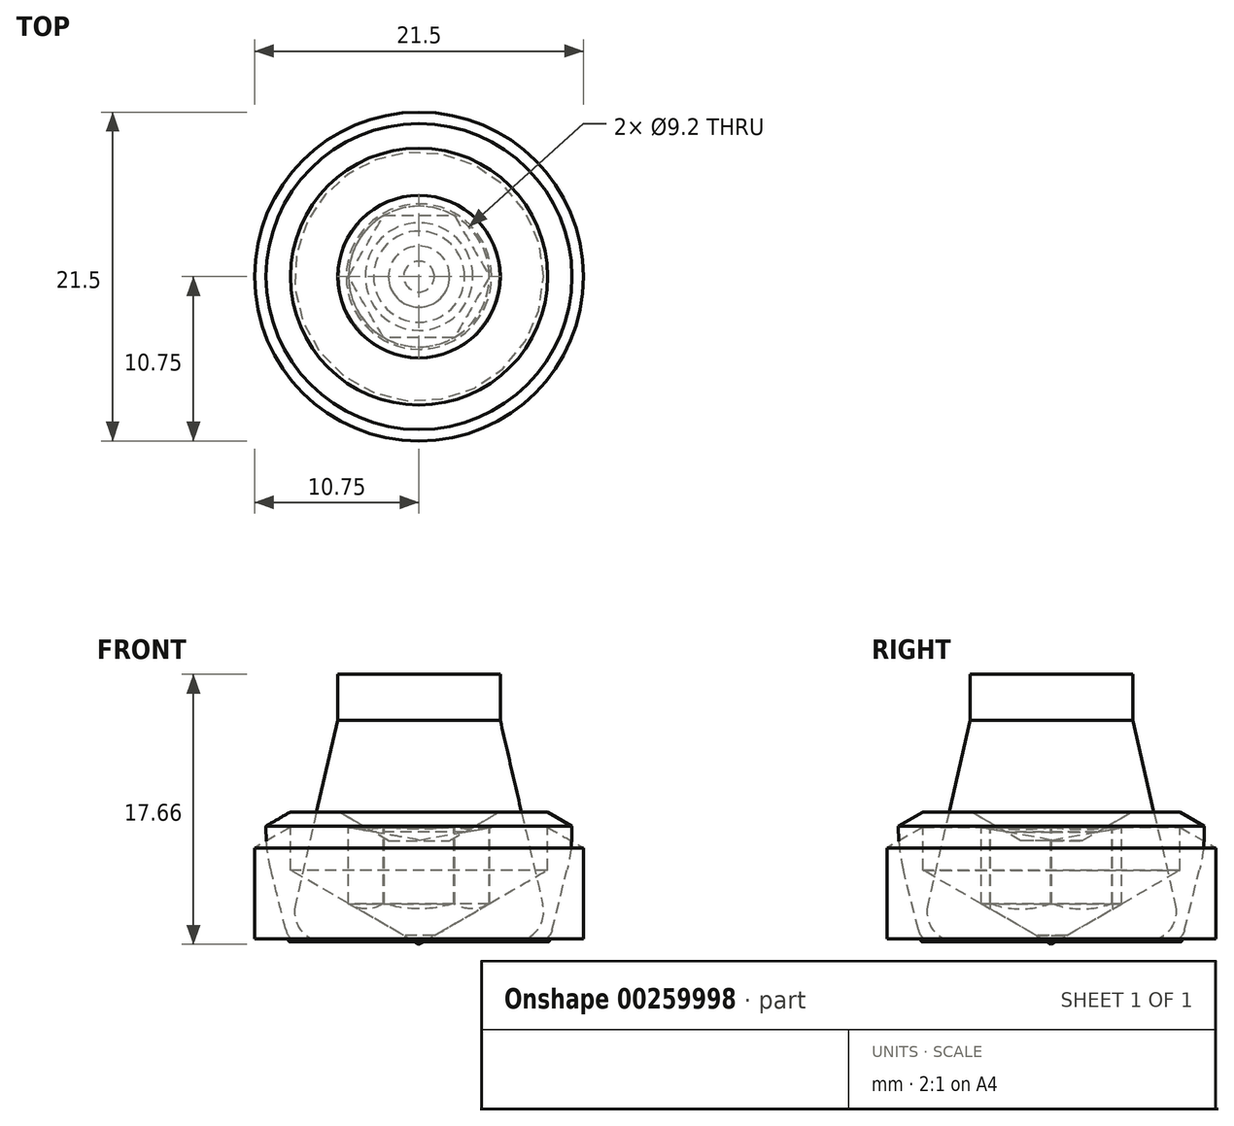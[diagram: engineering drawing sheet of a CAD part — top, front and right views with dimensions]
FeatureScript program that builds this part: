
annotation { "Feature Type Name" : "Feature", "Feature Type Description" : "" }
export const myFeature = defineFeature(function(context is Context, id is Id, definition is map)
    precondition{}
    {
        {
            var Q0;
            Q0=qCreatedBy(makeId("Front.planeOp"),FACE);
            var sketch = newSketch(context, id + "F0", { "sketchPlane" : qUnion([Q0])});
            skLineSegment(sketch, "E0", {"start": v(0, 0) * mm, "end": v(0, 0.42) * mm, "construction": true});
            skLineSegment(sketch, "E1", {"start": v(4.6, 7.5) * mm, "end": v(8.4, 7.5) * mm});
            skLineSegment(sketch, "E2", {"start": v(10.75, 6.14) * mm, "end": v(10.75, 0.2) * mm});
            skLineSegment(sketch, "E3", {"start": v(8.42, 0) * mm, "end": v(0, 0) * mm});
            skPoint(sketch, "E4.visualSharp", {"position": v(10.75, 7.5) * mm});
            skLineSegment(sketch, "E5", {"start": v(4.6, 7.5) * mm, "end": v(4.6, 2.5) * mm});
            skLineSegment(sketch, "E6", {"start": v(4.6, 2.5) * mm, "end": v(1, 0.42) * mm});
            skLineSegment(sketch, "E7", {"start": v(1, 0.42) * mm, "end": v(0, 0.42) * mm});
            skLineSegment(sketch, "E8", {"start": v(0, 0.42) * mm, "end": v(0, 0) * mm});
            skLineSegment(sketch, "E9", {"start": v(8.4, 7.5) * mm, "end": v(10.75, 6.14) * mm});
            skLineSegment(sketch, "E10", {"start": v(8.52, 0.07) * mm, "end": v(8.53, 0.13) * mm});
            skLineSegment(sketch, "E11", {"start": v(8.63, 0.2) * mm, "end": v(10.75, 0.2) * mm});
            skPoint(sketch, "E12.visualSharp", {"position": v(8.5, 0) * mm});
            skArc(sketch, "E12.filletArc", {"start": v(8.42, 0) * mm, "mid": v(8.48, 0.02) * mm, "end": v(8.52, 0.07) * mm});
            skPoint(sketch, "E13.visualSharp", {"position": v(8.55, 0.2) * mm});
            skArc(sketch, "E13.filletArc", {"start": v(8.63, 0.2) * mm, "mid": v(8.57, 0.18) * mm, "end": v(8.53, 0.13) * mm});
            skSolve(sketch);
        }
        {
            var Q0;
            Q0=qSketchRegion(id+"F0",true);
            var Q1;
            Q1=sQuery(id+"F0.wireOp",EDGE,"E8");
            revolve(context, id + "F1", {"entities" : qUnion([Q0]), "axis" : qUnion([Q1]), "revolveType" : RevolveType.FULL});
        }
        {
            var Q0;
            Q0=makeQuery(id+"F1.opRevolve","SWEPT_FACE",FACE,{"disambiguationData":[OSD([sQuery(id+"F0.wireOp",EDGE,"E1")])]});
            var sketch = newSketch(context, id + "F2", { "sketchPlane" : qUnion([Q0])});
            skCircle(sketch, "E14", {"center": v(0, 0) * mm, "radius": 4.6 * mm});
            skCircle(sketch, "E15.cCircle", {"center": v(0, 0) * mm, "radius": 4 * mm, "construction": true});
            skLineSegment(sketch, "E15.0", {"start": v(-2.3, 4) * mm, "end": v(2.3, 4) * mm});
            skLineSegment(sketch, "E15.1", {"start": v(2.3, 4) * mm, "end": v(4.62, 0) * mm});
            skLineSegment(sketch, "E15.2", {"start": v(4.62, 0) * mm, "end": v(2.3, -4) * mm});
            skLineSegment(sketch, "E15.3", {"start": v(2.3, -4) * mm, "end": v(-2.3, -4) * mm});
            skLineSegment(sketch, "E15.4", {"start": v(-2.3, -4) * mm, "end": v(-4.62, 0) * mm});
            skLineSegment(sketch, "E15.5", {"start": v(-4.62, 0) * mm, "end": v(-2.3, 4) * mm});
            skPoint(sketch, "E15.0.midPoint", {"position": v(0, 4) * mm});
            skSolve(sketch);
        }
        {
            var Q0;
            {var subQ0=sQuery(id+"F2.wireOp",EDGE,"E15.1");var subQ1=sQuery(id+"F2.wireOp",EDGE,"E14");var subQ2=makeQuery(id+"F2.imprint","INTERSECT",VERTEX,{"disambiguationData":[OD(0.0)],"derivedFrom":[subQ1,subQ0]});Q0=makeQuery(id+"F2.imprint","IMPRINT",FACE,{"disambiguationData":[TD([[makeQuery(id+"F2.imprint","IMPRINT",EDGE,{"disambiguationData":[TD([[subQ2,1.0]])],"derivedFrom":subQ1}),1.0]])]});}
            var Q1;
            {var subQ0=sQuery(id+"F2.wireOp",EDGE,"E15.1");var subQ1=sQuery(id+"F2.wireOp",EDGE,"E14");var subQ2=makeQuery(id+"F2.imprint","INTERSECT",VERTEX,{"disambiguationData":[OD(0.0)],"derivedFrom":[subQ1,subQ0]});Q1=makeQuery(id+"F2.imprint","IMPRINT",FACE,{"disambiguationData":[TD([[makeQuery(id+"F2.imprint","IMPRINT",EDGE,{"disambiguationData":[TD([[subQ2,-1.0]])],"derivedFrom":subQ1}),-1.0]])]});}
            var Q2;
            {var subQ0=sQuery(id+"F2.wireOp",EDGE,"E15.0");var subQ1=sQuery(id+"F2.wireOp",EDGE,"E14");var subQ2=makeQuery(id+"F2.imprint","INTERSECT",VERTEX,{"disambiguationData":[OD(0.0)],"derivedFrom":[subQ1,subQ0]});Q2=makeQuery(id+"F2.imprint","IMPRINT",FACE,{"disambiguationData":[TD([[makeQuery(id+"F2.imprint","IMPRINT",EDGE,{"disambiguationData":[TD([[subQ2,-1.0]])],"derivedFrom":subQ1}),1.0]])]});}
            var Q3;
            {var subQ0=sQuery(id+"F2.wireOp",EDGE,"E15.0");var subQ1=sQuery(id+"F2.wireOp",EDGE,"E14");var subQ2=makeQuery(id+"F2.imprint","INTERSECT",VERTEX,{"disambiguationData":[OD(1.0)],"derivedFrom":[subQ1,subQ0]});Q3=makeQuery(id+"F2.imprint","IMPRINT",FACE,{"disambiguationData":[TD([[makeQuery(id+"F2.imprint","IMPRINT",EDGE,{"disambiguationData":[TD([[subQ2,-1.0]])],"derivedFrom":subQ1}),-1.0]])]});}
            var Q4;
            {var subQ0=sQuery(id+"F2.wireOp",EDGE,"E15.5");var subQ1=sQuery(id+"F2.wireOp",EDGE,"E14");var subQ2=makeQuery(id+"F2.imprint","INTERSECT",VERTEX,{"disambiguationData":[OD(0.0)],"derivedFrom":[subQ1,subQ0]});Q4=makeQuery(id+"F2.imprint","IMPRINT",FACE,{"disambiguationData":[TD([[makeQuery(id+"F2.imprint","IMPRINT",EDGE,{"disambiguationData":[TD([[subQ2,-1.0]])],"derivedFrom":subQ1}),1.0]])]});}
            var Q5;
            {var subQ0=sQuery(id+"F2.wireOp",EDGE,"E15.5");var subQ1=sQuery(id+"F2.wireOp",EDGE,"E14");var subQ2=makeQuery(id+"F2.imprint","INTERSECT",VERTEX,{"disambiguationData":[OD(1.0)],"derivedFrom":[subQ1,subQ0]});Q5=makeQuery(id+"F2.imprint","IMPRINT",FACE,{"disambiguationData":[TD([[makeQuery(id+"F2.imprint","IMPRINT",EDGE,{"disambiguationData":[TD([[subQ2,-1.0]])],"derivedFrom":subQ1}),-1.0]])]});}
            var Q6;
            {var subQ0=sQuery(id+"F2.wireOp",EDGE,"E15.4");var subQ1=sQuery(id+"F2.wireOp",EDGE,"E14");var subQ2=makeQuery(id+"F2.imprint","INTERSECT",VERTEX,{"disambiguationData":[OD(0.0)],"derivedFrom":[subQ1,subQ0]});Q6=makeQuery(id+"F2.imprint","IMPRINT",FACE,{"disambiguationData":[TD([[makeQuery(id+"F2.imprint","IMPRINT",EDGE,{"disambiguationData":[TD([[subQ2,-1.0]])],"derivedFrom":subQ1}),1.0]])]});}
            var Q7;
            {var subQ0=sQuery(id+"F2.wireOp",EDGE,"E15.4");var subQ1=sQuery(id+"F2.wireOp",EDGE,"E14");var subQ2=makeQuery(id+"F2.imprint","INTERSECT",VERTEX,{"disambiguationData":[OD(1.0)],"derivedFrom":[subQ1,subQ0]});Q7=makeQuery(id+"F2.imprint","IMPRINT",FACE,{"disambiguationData":[TD([[makeQuery(id+"F2.imprint","IMPRINT",EDGE,{"disambiguationData":[TD([[subQ2,-1.0]])],"derivedFrom":subQ1}),-1.0]])]});}
            var Q8;
            {var subQ0=sQuery(id+"F2.wireOp",EDGE,"E15.3");var subQ1=sQuery(id+"F2.wireOp",EDGE,"E14");var subQ2=makeQuery(id+"F2.imprint","INTERSECT",VERTEX,{"disambiguationData":[OD(0.0)],"derivedFrom":[subQ1,subQ0]});Q8=makeQuery(id+"F2.imprint","IMPRINT",FACE,{"disambiguationData":[TD([[makeQuery(id+"F2.imprint","IMPRINT",EDGE,{"disambiguationData":[TD([[subQ2,-1.0]])],"derivedFrom":subQ1}),1.0]])]});}
            var Q9;
            {var subQ0=sQuery(id+"F2.wireOp",EDGE,"E15.3");var subQ1=sQuery(id+"F2.wireOp",EDGE,"E14");var subQ2=makeQuery(id+"F2.imprint","INTERSECT",VERTEX,{"disambiguationData":[OD(1.0)],"derivedFrom":[subQ1,subQ0]});Q9=makeQuery(id+"F2.imprint","IMPRINT",FACE,{"disambiguationData":[TD([[makeQuery(id+"F2.imprint","IMPRINT",EDGE,{"disambiguationData":[TD([[subQ2,-1.0]])],"derivedFrom":subQ1}),-1.0]])]});}
            var Q10;
            {var subQ0=sQuery(id+"F2.wireOp",EDGE,"E15.2");var subQ1=sQuery(id+"F2.wireOp",EDGE,"E14");var subQ2=makeQuery(id+"F2.imprint","INTERSECT",VERTEX,{"disambiguationData":[OD(0.0)],"derivedFrom":[subQ1,subQ0]});Q10=makeQuery(id+"F2.imprint","IMPRINT",FACE,{"disambiguationData":[TD([[makeQuery(id+"F2.imprint","IMPRINT",EDGE,{"disambiguationData":[TD([[subQ2,-1.0]])],"derivedFrom":subQ1}),1.0]])]});}
            var Q11;
            {var subQ0=sQuery(id+"F2.wireOp",EDGE,"E15.1");var subQ1=sQuery(id+"F2.wireOp",EDGE,"E14");var subQ2=makeQuery(id+"F2.imprint","INTERSECT",VERTEX,{"disambiguationData":[OD(1.0)],"derivedFrom":[subQ1,subQ0]});Q11=makeQuery(id+"F2.imprint","IMPRINT",FACE,{"disambiguationData":[TD([[makeQuery(id+"F2.imprint","IMPRINT",EDGE,{"disambiguationData":[TD([[subQ2,1.0]])],"derivedFrom":subQ1}),-1.0]])]});}
            var Q12;
            Q12=makeQuery(id+"F1.opRevolve","SWEPT_FACE",FACE,{"disambiguationData":[OSD([sQuery(id+"F0.wireOp",EDGE,"E6")])]});
            extrude(context, id + "F3", {"entities" : qUnion([Q0, Q1, Q2, Q3, Q4, Q5, Q6, Q7, Q8, Q9, Q10, Q11]), "operationType" : NewBodyOperationType.ADD, "endBound" : BoundingType.UP_TO_SURFACE, "oppositeDirection" : true, "endBoundEntityFace" : qUnion([Q12]), "depth" : 25 * mm});
        }
        {
            var Q0;
            Q0=makeQuery(id+"F3.boolean.opBoolean","MERGE",FACE,{"derivedFrom":[makeQuery(id+"F1.opRevolve","SWEPT_FACE",FACE,{"disambiguationData":[OSD([sQuery(id+"F0.wireOp",EDGE,"E1")])]}),makeQuery(id+"F3.opExtrude","CAP_FACE",FACE,{"disambiguationData":[OSD([sQuery(id+"F2.wireOp",EDGE,"axiUSiGf-8ymJ-Ezfh-tHsk-ULXXzRlxOoBz"),sQuery(id+"F2.wireOp",EDGE,"WrdyBTnM-XU54-uk96-2Sjo-h1HHDxb1zyqn"),sQuery(id+"F2.wireOp",EDGE,"7iNK7enz-fUzD-7EQp-KRCh-aPKnPlRcPdaK"),sQuery(id+"F2.wireOp",EDGE,"e7c95674-c634-4135-8625-61586754ee6a.1.0"),sQuery(id+"F2.wireOp",EDGE,"e7c95674-c634-4135-8625-61586754ee6a.1.1"),sQuery(id+"F2.wireOp",EDGE,"e7c95674-c634-4135-8625-61586754ee6a.1.2"),sQuery(id+"F2.wireOp",EDGE,"e7c95674-c634-4135-8625-61586754ee6a.2.0"),sQuery(id+"F2.wireOp",EDGE,"e7c95674-c634-4135-8625-61586754ee6a.2.1"),sQuery(id+"F2.wireOp",EDGE,"e7c95674-c634-4135-8625-61586754ee6a.2.2"),sQuery(id+"F2.wireOp",EDGE,"e7c95674-c634-4135-8625-61586754ee6a.3.0"),sQuery(id+"F2.wireOp",EDGE,"e7c95674-c634-4135-8625-61586754ee6a.3.1"),sQuery(id+"F2.wireOp",EDGE,"e7c95674-c634-4135-8625-61586754ee6a.3.2"),sQuery(id+"F2.wireOp",EDGE,"e7c95674-c634-4135-8625-61586754ee6a.4.0"),sQuery(id+"F2.wireOp",EDGE,"e7c95674-c634-4135-8625-61586754ee6a.4.1"),sQuery(id+"F2.wireOp",EDGE,"e7c95674-c634-4135-8625-61586754ee6a.4.2"),sQuery(id+"F2.wireOp",EDGE,"e7c95674-c634-4135-8625-61586754ee6a.5.0"),sQuery(id+"F2.wireOp",EDGE,"e7c95674-c634-4135-8625-61586754ee6a.5.1"),sQuery(id+"F2.wireOp",EDGE,"e7c95674-c634-4135-8625-61586754ee6a.5.2"),sQuery(id+"F2.wireOp",EDGE,"c34f7dbc-1fd9-48ae-9599-0fb72b0d65de.filletArc"),sQuery(id+"F2.wireOp",EDGE,"5fecc0f4-c57f-42b8-a97f-f8fbf54cf4db.filletArc"),sQuery(id+"F2.wireOp",EDGE,"b077568f-b672-48a6-a184-fa18c1575088.filletArc"),sQuery(id+"F2.wireOp",EDGE,"4c4ba650-eb3b-40a6-a5b6-7d0bcd232093.filletArc"),sQuery(id+"F2.wireOp",EDGE,"b016cc09-0b8d-437b-9508-1d7630c9d4ff.filletArc"),sQuery(id+"F2.wireOp",EDGE,"d5479cb3-145b-41e2-b586-5ab3f6452500.filletArc"),sQuery(id+"F2.wireOp",EDGE,"E14")])],"isStart":true})]});
            var sketch = newSketch(context, id + "F4", { "sketchPlane" : qUnion([Q0])});
            skCircle(sketch, "E16", {"center": v(0, 0) * mm, "radius": 4.75 * mm});
            skSolve(sketch);
        }
        {
            var Q0;
            Q0=qSketchRegion(id+"F4",true);
            extrude(context, id + "F5", {"entities" : qUnion([Q0]), "operationType" : NewBodyOperationType.REMOVE, "oppositeDirection" : true, "depth" : 1 * mm, "hasDraft" : true, "draftAngle" : 80 * degree, "draftPullDirection" : true});
        }
        {
            var Q0;
            Q0=qCreatedBy(makeId("Front.planeOp"),FACE);
            var sketch = newSketch(context, id + "F6", { "sketchPlane" : qUnion([Q0])});
            skLineSegment(sketch, "E17", {"start": v(0, 0) * mm, "end": v(0, 17.5) * mm, "construction": true});
            skLineSegment(sketch, "E18", {"start": v(0, 17.5) * mm, "end": v(5.3, 17.5) * mm});
            skLineSegment(sketch, "E19", {"start": v(5.3, 17.5) * mm, "end": v(5.3, 14.5) * mm});
            skLineSegment(sketch, "E20", {"start": v(5.3, 14.5) * mm, "end": v(8.1, 2.45) * mm});
            skLineSegment(sketch, "E21", {"start": v(6.14, 0) * mm, "end": v(0, 0) * mm});
            skLineSegment(sketch, "E22", {"start": v(0, 17.5) * mm, "end": v(0, 0) * mm});
            skPoint(sketch, "E23.visualSharp", {"position": v(8.66, 0) * mm});
            skArc(sketch, "E23.filletArc", {"start": v(6.14, 0) * mm, "mid": v(7.7, 0.75) * mm, "end": v(8.1, 2.45) * mm});
            skSolve(sketch);
        }
        {
            var Q0;
            Q0=qSketchRegion(id+"F6",true);
            var Q1;
            Q1=sQuery(id+"F6.wireOp",EDGE,"E22");
            revolve(context, id + "F7", {"entities" : qUnion([Q0]), "axis" : qUnion([Q1]), "revolveType" : RevolveType.FULL});
        }
        {
            var Q0;
            Q0=qCreatedBy(makeId("Front.planeOp"),FACE);
            var sketch = newSketch(context, id + "F8", { "sketchPlane" : qUnion([Q0])});
            skLineSegment(sketch, "E24", {"start": v(0, 0) * mm, "end": v(0, 6.62) * mm});
            skLineSegment(sketch, "E25", {"start": v(9.68, 4.7) * mm, "end": v(8.7, 0.76) * mm});
            skLineSegment(sketch, "E26", {"start": v(7.72, 0) * mm, "end": v(0, 0) * mm});
            skLineSegment(sketch, "E27", {"start": v(0, 6.62) * mm, "end": v(0, 0) * mm, "construction": true});
            skLineSegment(sketch, "E28", {"start": v(0, 6.62) * mm, "end": v(2, 6.62) * mm});
            skLineSegment(sketch, "E29", {"start": v(2, 6.62) * mm, "end": v(5.25, 8.5) * mm});
            skLineSegment(sketch, "E30", {"start": v(5.25, 8.5) * mm, "end": v(8.4, 8.5) * mm});
            skArc(sketch, "E31.filletArc", {"start": v(9.68, 4.7) * mm, "mid": v(9.93, 6.13) * mm, "end": v(10, 7.58) * mm});
            skLineSegment(sketch, "E32", {"start": v(9.68, 4.7) * mm, "end": v(10, 6) * mm, "construction": true});
            skLineSegment(sketch, "E33", {"start": v(8.4, 8.5) * mm, "end": v(10, 7.58) * mm});
            skPoint(sketch, "E34.visualSharp", {"position": v(8.5, 0) * mm});
            skArc(sketch, "E34.filletArc", {"start": v(7.72, 0) * mm, "mid": v(8.34, 0.21) * mm, "end": v(8.7, 0.76) * mm});
            skSolve(sketch);
        }
        {
            var Q0;
            Q0=qSketchRegion(id+"F8",true);
            var Q1;
            Q1=sQuery(id+"F8.wireOp",EDGE,"E24");
            revolve(context, id + "F9", {"entities" : qUnion([Q0]), "axis" : qUnion([Q1]), "revolveType" : RevolveType.FULL});
        }
    });
